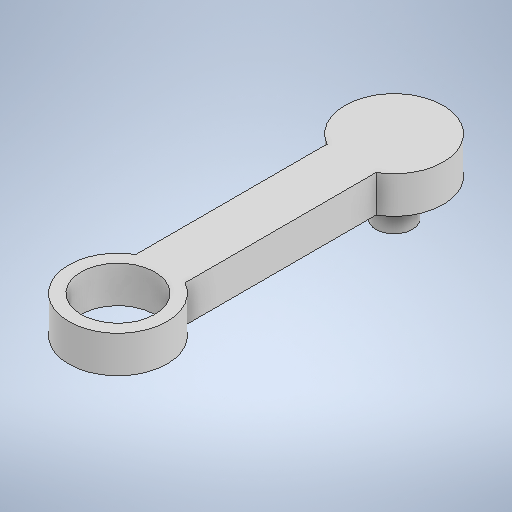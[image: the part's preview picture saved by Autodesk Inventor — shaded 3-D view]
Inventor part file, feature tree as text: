
AUTODESK INVENTOR PART (.ipt)
format: ipt  version: 2025.1 (Build 291241000, 241)  size: 252,928 bytes
history: native  units: mm
features: extrude x2, sketch x1
ambient origin geometry x8: Origin, YZ Plane, XZ Plane, XY Plane, X Axis, Y Axis, Z Axis, Center Point
bodies: Solid1 (feature_tree)
feature tree (3):
  sketch  "Sketch1"  dims[d0=45.0mm d1=22.5mm d2=8.0mm d3=4.0mm d6=8.0mm d7=8.0mm d8=12.0mm d9=6.0mm d10=6.0mm d11=0.0mm d12=12.0mm d13=0.0mm]
  extrude  "Extrusion1"  Depth=22.5mm
  extrude  "Extrusion2"  Depth=8.0mm
